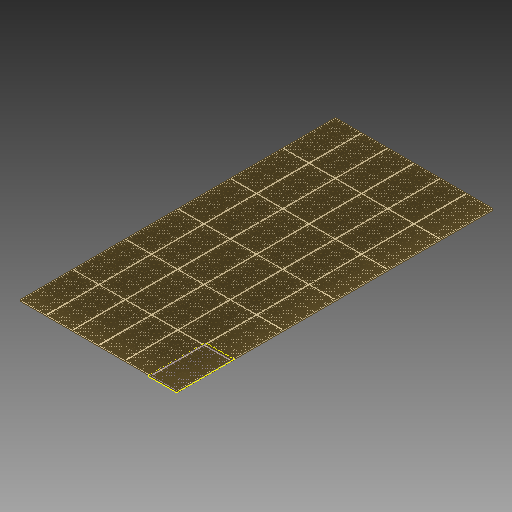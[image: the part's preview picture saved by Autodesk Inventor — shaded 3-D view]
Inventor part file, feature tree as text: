
AUTODESK INVENTOR PART (.ipt)
format: ipt  version: 2018 (Build 220112000, 112)  size: 16,924,672 bytes
history: native  units: in
note: dims shown in document units (in); Inventor stores cm internally (conversion verified against a paired STEP export)
features: extrude x2, sketch x2, plane x1, pattern_linear x1
ambient origin geometry x8: Origin, YZ Plane, XZ Plane, XY Plane, X Axis, Y Axis, Z Axis, Center Point
bodies: Solid1 (feature_tree)
feature tree (6):
  extrude  "Extrusion1"  Depth=240.0in
  extrude  "Extrusion2"  Depth=10.0in
  plane  "Work Plane1"
  pattern_linear  "Rectangular Pattern1"  Spacing1=10.0in  [1 undecoded]
  sketch  "Sketch1"  dims[d0=120.0in d1=240.0in]
  sketch  "Sketch2"  dims[d2=7.0in d3=0.0in d4=10.0in d5=10.0in d6=8.2677in d8=11.0in d9=3.937in d11=11.0in d14=1.0in d15=0.0in d16=90.0deg d17=2.3622in d19=120.0in d29=2.3622in d31=240.0in]
note: 1 required parameter value undecoded (feature->parameter linkage not recoverable at this tier; creation-order binding heuristic only, values carry confidence <= 0.55)
